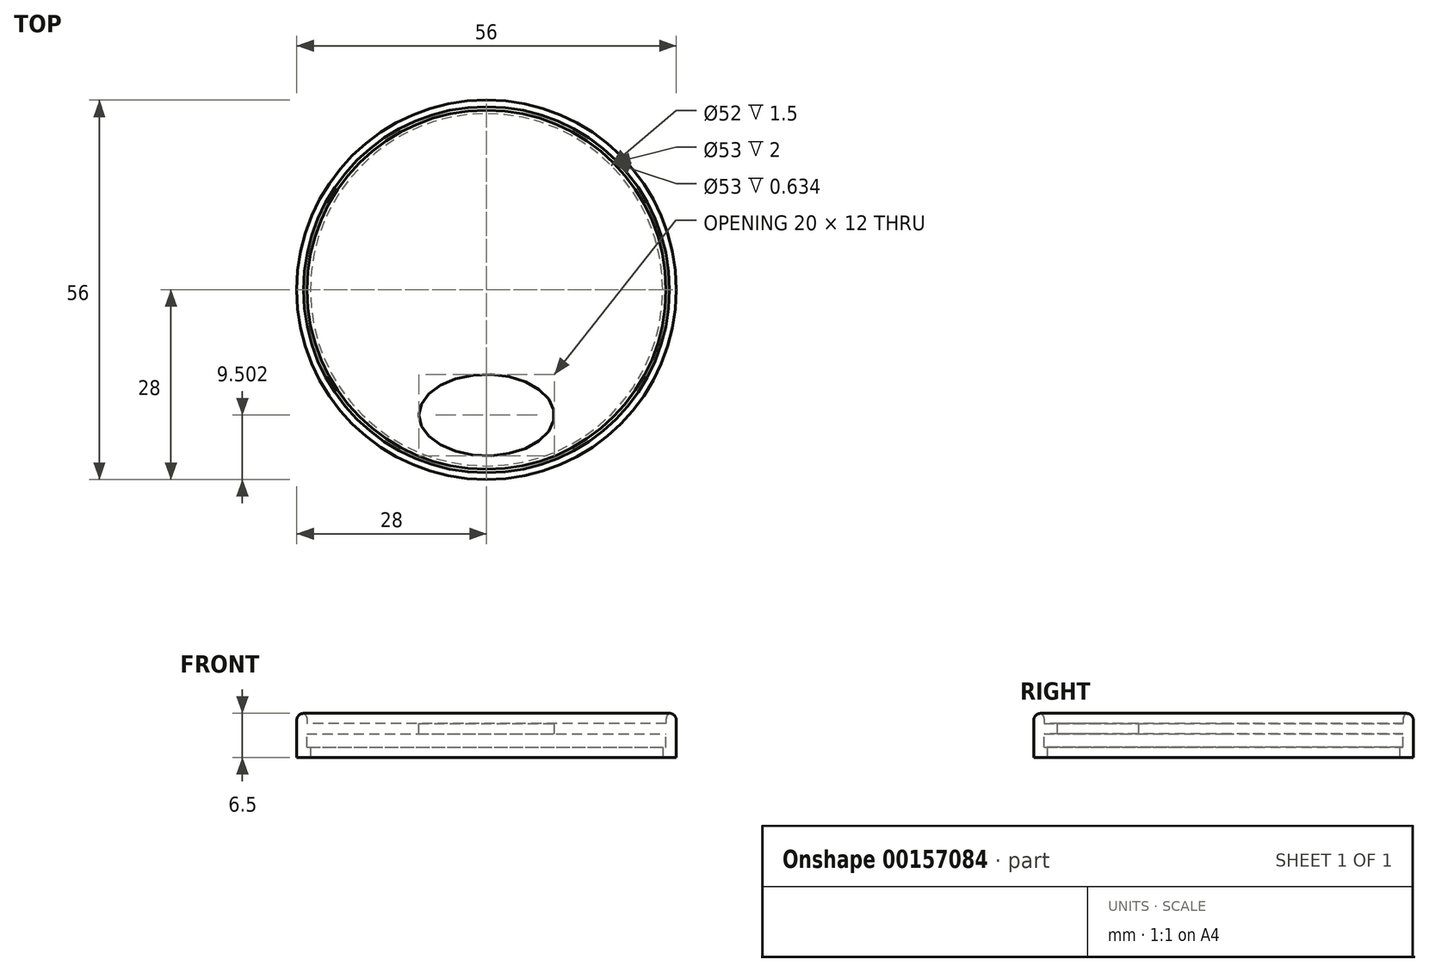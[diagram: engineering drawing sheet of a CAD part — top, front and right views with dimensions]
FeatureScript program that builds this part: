
annotation { "Feature Type Name" : "Feature", "Feature Type Description" : "" }
export const myFeature = defineFeature(function(context is Context, id is Id, definition is map)
    precondition{}
    {
        {
            var Q0;
            Q0=qCreatedBy(makeId("Top.planeOp"),FACE);
            var sketch = newSketch(context, id + "F0", { "sketchPlane" : qUnion([Q0])});
            skCircle(sketch, "E0", {"center": v(0, 0) * mm, "radius": 28 * mm});
            skSolve(sketch);
        }
        {
            var Q0;
            Q0 = qSketchRegion(id + "F0", true);
            extrude(context, id + "F1", {"entities" : qUnion([Q0]), "depth" : 5 * mm});
        }
        {
            var Q0;
            Q0=makeQuery(id+"F1.opExtrude","CAP_FACE",FACE,{"disambiguationData":[OSD([sQuery(id+"F0.wireOp",EDGE,"E0")])],"isStart":true});
            var sketch = newSketch(context, id + "F2", { "sketchPlane" : qUnion([Q0])});
            skCircle(sketch, "E1", {"center": v(0, 0) * mm, "radius": 26 * mm});
            skSolve(sketch);
        }
        {
            var Q0;
            Q0 = qSketchRegion(id + "F2", true);
            extrude(context, id + "F3", {"entities" : qUnion([Q0]), "operationType" : NewBodyOperationType.REMOVE, "oppositeDirection" : true, "depth" : 3.5 * mm});
        }
        {
            var Q0;
            Q0=makeQuery(id+"F3.boolean.opBoolean","COPY",FACE,{"derivedFrom":makeQuery(id+"F3.opExtrude","CAP_FACE",FACE,{"disambiguationData":[OSD([sQuery(id+"F2.wireOp",EDGE,"E1")])],"isStart":false})});
            var sketch = newSketch(context, id + "F4", { "sketchPlane" : qUnion([Q0])});
            skCircle(sketch, "E2", {"center": v(0, 0) * mm, "radius": 26.5 * mm});
            skSolve(sketch);
        }
        {
            var Q0;
            Q0 = qSketchRegion(id + "F4", true);
            extrude(context, id + "F5", {"entities" : qUnion([Q0]), "operationType" : NewBodyOperationType.REMOVE, "depth" : 2 * mm});
        }
        {
            var Q0;
            Q0=makeQuery(id+"F1.opExtrude","CAP_FACE",FACE,{"disambiguationData":[OSD([sQuery(id+"F0.wireOp",EDGE,"E0")])],"isStart":false});
            var sketch = newSketch(context, id + "F6", { "sketchPlane" : qUnion([Q0])});
            skEllipse(sketch, "E3", {"center": v(0, -18.5) * mm, "majorRadius": 10 * mm, "minorRadius": 6 * mm, "majorAxis": v(-1, 0)});
            skSolve(sketch);
        }
        {
            var Q0;
            Q0 = qSketchRegion(id + "F6", true);
            extrude(context, id + "F7", {"entities" : qUnion([Q0]), "operationType" : NewBodyOperationType.REMOVE, "oppositeDirection" : true, "depth" : 6 * mm});
        }
        {
            var Q0;
            Q0=makeQuery(id+"F1.opExtrude","CAP_FACE",FACE,{"disambiguationData":[OSD([sQuery(id+"F0.wireOp",EDGE,"E0")])],"isStart":false});
            var sketch = newSketch(context, id + "F8", { "sketchPlane" : qUnion([Q0])});
            skCircle(sketch, "E4", {"center": v(0, 0) * mm, "radius": 28 * mm});
            skCircle(sketch, "E5", {"center": v(0, 0) * mm, "radius": 26.5 * mm});
            skSolve(sketch);
        }
        {
            var Q0;
            Q0 = qSketchRegion(id + "F8", true);
            extrude(context, id + "F9", {"entities" : qUnion([Q0]), "operationType" : NewBodyOperationType.ADD, "depth" : 1.5 * mm});
        }
        {
            var Q0;
            Q0=makeQuery(id+"F9.opExtrude","CAP_EDGE",EDGE,{"disambiguationData":[OSD([sQuery(id+"F8.wireOp",EDGE,"E4")])],"isStart":false});
            fillet(context, id + "F10", {"entities" : qUnion([Q0]), "radius" : 1 * mm, "tangentPropagation" : true, "allowEdgeOverflow" : false});
        }
        {
            var Q0;
            Q0=makeQuery(id+"F9.opExtrude","CAP_EDGE",EDGE,{"disambiguationData":[OSD([sQuery(id+"F8.wireOp",EDGE,"E5")])],"isStart":false});
            fillet(context, id + "F11", {"entities" : qUnion([Q0]), "radius" : 1 * mm, "tangentPropagation" : true, "allowEdgeOverflow" : false});
        }
    });
